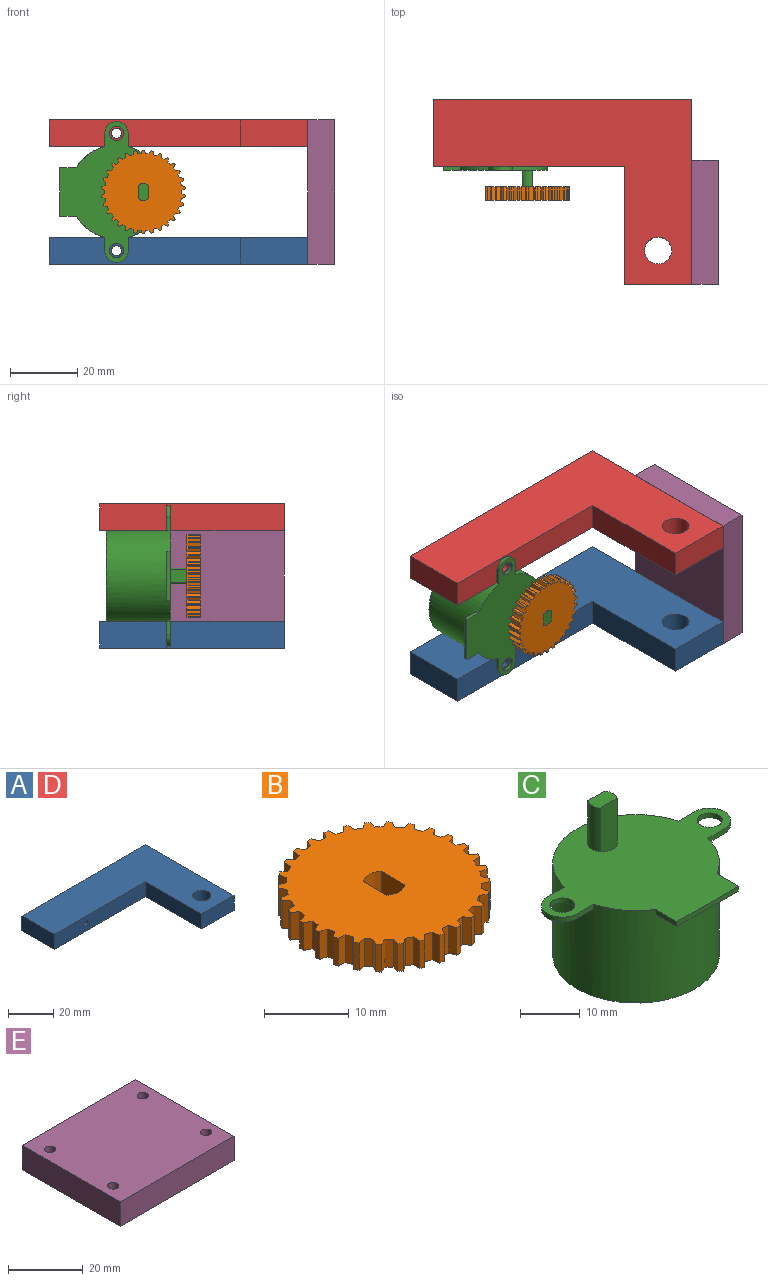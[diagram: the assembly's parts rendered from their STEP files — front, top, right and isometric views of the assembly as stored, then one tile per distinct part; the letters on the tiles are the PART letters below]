
ASSEMBLY  parts=5 mates=4
PART A: 10 faces, bbox 77x55x8 mm
  f0: plane 20x8mm, normal (0,-1,0), area 160mm2, adj f1,f5,f6,f7
  f1: plane 55x8mm, normal (1,0,0), area 440mm2, adj f0,f2,f6,f7
  f2: plane 77x8mm, normal (0,1,0), area 608.9mm2, adj f1,f3,f6,f7,f8
  f3: plane 20x8mm, normal (-1,0,0), area 160mm2, adj f2,f4,f6,f7
  f4: plane 57x8mm, normal (0,-1,0), area 448.9mm2, adj f3,f5,f6,f7,f8
  f5: plane 35x8mm, normal (-1,0,0), area 280mm2, adj f0,f4,f6,f7
  f6: plane 77x55mm, normal (0,0,1), area 2189.7mm2, adj f0,f1,f2,f3,f4,f5,f9
  f7: plane 77x55mm, normal (0,0,-1), area 2189.7mm2, adj f0,f1,f2,f3,f4,f5,f9
  f8: cylinder r=1.5mm len=20mm, axis (0,1,0), area 188.5mm2, adj f2,f4
  f9: cylinder r=4mm len=8mm, axis (0,0,-1), area 201.1mm2, adj f6,f7
PART B: 126 faces, bbox 24.9x25x4 mm
  f0: cylinder r=12.5mm len=4mm, axis (0,0,-1), area 2.6mm2, adj f30,f35,f118,f123
  f1: cylinder r=12.5mm len=4mm, axis (0,0,-1), area 2.6mm2, adj f30,f35,f54,f124
  f2: cylinder r=12.5mm len=4mm, axis (0,0,-1), area 2.6mm2, adj f30,f35,f61,f120
  f3: cylinder r=12.5mm len=4mm, axis (0,0,-1), area 2.6mm2, adj f30,f35,f111,f121
  f4: cylinder r=12.5mm len=4mm, axis (0,0,-1), area 2.6mm2, adj f30,f35,f103,f117
  f5: cylinder r=12.5mm len=4mm, axis (0,0,-1), area 2.6mm2, adj f30,f35,f100,f114
  f6: cylinder r=12.5mm len=4mm, axis (0,0,-1), area 2.6mm2, adj f30,f35,f84,f115
  f7: cylinder r=12.5mm len=4mm, axis (0,0,-1), area 2.6mm2, adj f30,f35,f39,f112
  f8: cylinder r=12.5mm len=4mm, axis (0,0,-1), area 2.6mm2, adj f30,f35,f82,f108
  f9: cylinder r=12.5mm len=4mm, axis (0,0,-1), area 2.6mm2, adj f30,f35,f78,f109
  f10: cylinder r=12.5mm len=4mm, axis (0,0,-1), area 2.6mm2, adj f30,f35,f73,f105
  f11: cylinder r=12.5mm len=4mm, axis (0,0,-1), area 2.6mm2, adj f30,f35,f45,f106
  f12: cylinder r=12.5mm len=4mm, axis (0,0,-1), area 2.6mm2, adj f30,f35,f67,f102
  f13: cylinder r=12.5mm len=4mm, axis (0,0,-1), area 2.6mm2, adj f30,f35,f79,f99
  f14: cylinder r=12.5mm len=4mm, axis (0,0,-1), area 2.6mm2, adj f30,f35,f37,f96
  f15: cylinder r=12.5mm len=4mm, axis (0,0,-1), area 2.6mm2, adj f30,f35,f87,f97
  f16: cylinder r=12.5mm len=4mm, axis (0,0,-1), area 2.6mm2, adj f30,f35,f55,f93
  f17: cylinder r=12.5mm len=4mm, axis (0,0,-1), area 2.6mm2, adj f30,f35,f48,f94
  f18: cylinder r=12.5mm len=4mm, axis (0,0,-1), area 2.6mm2, adj f30,f35,f43,f90
  f19: cylinder r=12.5mm len=4mm, axis (0,0,-1), area 2.6mm2, adj f30,f35,f69,f91
  f20: cylinder r=12.5mm len=4mm, axis (0,0,-1), area 2.6mm2, adj f30,f35,f63,f88
  f21: cylinder r=12.5mm len=4mm, axis (0,0,-1), area 2.6mm2, adj f30,f35,f36,f85
  f22: cylinder r=12.5mm len=4mm, axis (0,0,-1), area 2.6mm2, adj f30,f35,f52,f81
  f23: cylinder r=12.5mm len=4mm, axis (0,0,-1), area 2.6mm2, adj f30,f35,f40,f75
  f24: cylinder r=12.5mm len=4mm, axis (0,0,-1), area 2.6mm2, adj f30,f35,f57,f76
  f25: cylinder r=12.5mm len=4mm, axis (0,0,-1), area 2.6mm2, adj f30,f35,f49,f72
  f26: cylinder r=12.5mm len=4mm, axis (0,0,-1), area 2.6mm2, adj f30,f35,f66,f70
  f27: cylinder r=12.5mm len=4mm, axis (0,0,-1), area 2.6mm2, adj f30,f35,f42,f64
  f28: cylinder r=12.5mm len=4mm, axis (0,0,-1), area 2.6mm2, adj f30,f35,f46,f60
  f29: cylinder r=12.5mm len=4mm, axis (0,0,-1), area 2.6mm2, adj f30,f35,f51,f58
  f30: plane 25x24.92mm, normal (0,0,1), area 432.6mm2, adj f0,f1,f2,f3,f4,f5,f6,f7
  f31: cylinder r=2.5mm len=4mm, axis (0,0,-1), area 12.9mm2, adj f30,f32,f34,f35
  f32: plane 4x4mm, normal (-1,0,0), area 16mm2, adj f30,f31,f33,f35
  f33: cylinder r=2.5mm len=4mm, axis (0,0,-1), area 12.9mm2, adj f30,f32,f34,f35
  f34: plane 4x4mm, normal (1,0,0), area 16mm2, adj f30,f31,f33,f35
  f35: plane 25x24.92mm, normal (0,0,-1), area 432.6mm2, adj f0,f1,f2,f3,f4,f5,f6,f7
  f36: plane 4x1.04mm, normal (-0.96,-0.27,0), area 4.3mm2, adj f21,f30,f35,f38
  f37: plane 4x1mm, normal (0.37,0.93,0), area 4.3mm2, adj f14,f30,f35,f38
  f38: plane 4x0.74mm, normal (-0.67,0.74,0), area 4mm2, adj f30,f35,f36,f37
  f39: plane 4x1.04mm, normal (0.25,0.97,0), area 4.3mm2, adj f7,f30,f35,f41
  f40: plane 4x0.84mm, normal (0.62,-0.78,0), area 4.3mm2, adj f23,f30,f35,f41
  f41: plane 4x0.98mm, normal (0.98,0.21,0), area 4mm2, adj f30,f35,f39,f40
  f42: plane 4x0.96mm, normal (-0.45,-0.89,0), area 4.3mm2, adj f27,f30,f35,f44
  f43: plane 4x0.96mm, normal (-0.45,0.89,0), area 4.3mm2, adj f18,f30,f35,f44
  f44: plane 4x1mm, normal (-1,0,0), area 4mm2, adj f30,f35,f42,f43
  f45: plane 4x0.95mm, normal (0.89,0.46,0), area 4.3mm2, adj f11,f30,f35,f47
  f46: plane 4x1.06mm, normal (-0.16,-0.99,0), area 4.3mm2, adj f28,f30,f35,f47
  f47: plane 4x0.81mm, normal (0.81,-0.59,0), area 4mm2, adj f30,f35,f45,f46
  f48: plane 4x1.06mm, normal (0.99,-0.15,0), area 4.3mm2, adj f17,f30,f35,f50
  f49: plane 4x0.77mm, normal (-0.71,-0.7,0), area 4.3mm2, adj f25,f30,f35,f50
  f50: plane 4x0.95mm, normal (0.31,-0.95,0), area 4mm2, adj f30,f35,f48,f49
  f51: plane 4x1mm, normal (-0.37,0.93,0), area 4.3mm2, adj f29,f30,f35,f53
  f52: plane 4x1.04mm, normal (0.96,-0.27,0), area 4.3mm2, adj f22,f30,f35,f53
  f53: plane 4x0.74mm, normal (0.67,0.74,0), area 4mm2, adj f30,f35,f51,f52
  f54: plane 4x0.91mm, normal (0.84,-0.54,0), area 4.3mm2, adj f1,f30,f35,f56
  f55: plane 4x1.01mm, normal (-0.94,-0.35,0), area 4.3mm2, adj f16,f30,f35,f56
  f56: plane 4x0.99mm, normal (-0.1,-0.99,0), area 4mm2, adj f30,f35,f54,f55
  f57: plane 4x1.06mm, normal (-0.16,0.99,0), area 4.3mm2, adj f24,f30,f35,f59
  f58: plane 4x0.95mm, normal (0.89,-0.46,0), area 4.3mm2, adj f29,f30,f35,f59
  f59: plane 4x0.81mm, normal (0.81,0.59,0), area 4mm2, adj f30,f35,f57,f58
  f60: plane 4x0.83mm, normal (0.77,0.64,0), area 4.3mm2, adj f28,f30,f35,f62
  f61: plane 4x1.07mm, normal (0.04,-1,0), area 4.3mm2, adj f2,f30,f35,f62
  f62: plane 4x0.91mm, normal (0.91,-0.41,0), area 4mm2, adj f30,f35,f60,f61
  f63: plane 4x0.84mm, normal (-0.62,-0.78,0), area 4.3mm2, adj f20,f30,f35,f65
  f64: plane 4x1.04mm, normal (-0.25,0.97,0), area 4.3mm2, adj f27,f30,f35,f65
  f65: plane 4x0.98mm, normal (-0.98,0.21,0), area 4mm2, adj f30,f35,f63,f64
  f66: plane 4x1.06mm, normal (0.16,-0.99,0), area 4.3mm2, adj f26,f30,f35,f68
  f67: plane 4x0.95mm, normal (-0.89,0.46,0), area 4.3mm2, adj f12,f30,f35,f68
  f68: plane 4x0.81mm, normal (-0.81,-0.59,0), area 4mm2, adj f30,f35,f66,f67
  f69: plane 4x1.07mm, normal (-0.04,-1,0), area 4.3mm2, adj f19,f30,f35,f71
  f70: plane 4x0.83mm, normal (-0.77,0.64,0), area 4.3mm2, adj f26,f30,f35,f71
  f71: plane 4x0.91mm, normal (-0.91,-0.41,0), area 4mm2, adj f30,f35,f69,f70
  f72: plane 4x1.07mm, normal (1,0.06,0), area 4.3mm2, adj f25,f30,f35,f74
  f73: plane 4x0.9mm, normal (-0.55,-0.83,0), area 4.3mm2, adj f10,f30,f35,f74
  f74: plane 4x0.87mm, normal (0.5,-0.87,0), area 4mm2, adj f30,f35,f72,f73
  f75: plane 4x1.07mm, normal (0.04,1,0), area 4.3mm2, adj f23,f30,f35,f77
  f76: plane 4x0.83mm, normal (0.77,-0.64,0), area 4.3mm2, adj f24,f30,f35,f77
  f77: plane 4x0.91mm, normal (0.91,0.41,0), area 4mm2, adj f30,f35,f75,f76
  f78: plane 4x0.91mm, normal (-0.84,0.54,0), area 4.3mm2, adj f9,f30,f35,f80
  f79: plane 4x1.01mm, normal (0.94,0.35,0), area 4.3mm2, adj f13,f30,f35,f80
  f80: plane 4x0.99mm, normal (0.1,0.99,0), area 4mm2, adj f30,f35,f78,f79
  f81: plane 4x0.9mm, normal (-0.55,0.83,0), area 4.3mm2, adj f22,f30,f35,f83
  f82: plane 4x1.07mm, normal (1,-0.06,0), area 4.3mm2, adj f8,f30,f35,f83
  f83: plane 4x0.87mm, normal (0.5,0.87,0), area 4mm2, adj f30,f35,f81,f82
  f84: plane 4x1.07mm, normal (-1,-0.06,0), area 4.3mm2, adj f6,f30,f35,f86
  f85: plane 4x0.9mm, normal (0.55,0.83,0), area 4.3mm2, adj f21,f30,f35,f86
  f86: plane 4x0.87mm, normal (-0.5,0.87,0), area 4mm2, adj f30,f35,f84,f85
  f87: plane 4x0.83mm, normal (-0.77,-0.64,0), area 4.3mm2, adj f15,f30,f35,f89
  f88: plane 4x1.07mm, normal (-0.04,1,0), area 4.3mm2, adj f20,f30,f35,f89
  f89: plane 4x0.91mm, normal (-0.91,0.41,0), area 4mm2, adj f30,f35,f87,f88
  f90: plane 4x1.04mm, normal (-0.25,-0.97,0), area 4.3mm2, adj f18,f30,f35,f92
  f91: plane 4x0.84mm, normal (-0.62,0.78,0), area 4.3mm2, adj f19,f30,f35,f92
  f92: plane 4x0.98mm, normal (-0.98,-0.21,0), area 4mm2, adj f30,f35,f90,f91
  f93: plane 4x1.01mm, normal (0.94,-0.35,0), area 4.3mm2, adj f16,f30,f35,f95
  f94: plane 4x0.91mm, normal (-0.84,-0.54,0), area 4.3mm2, adj f17,f30,f35,f95
  f95: plane 4x0.99mm, normal (0.1,-0.99,0), area 4mm2, adj f30,f35,f93,f94
  f96: plane 4x0.95mm, normal (-0.89,-0.46,0), area 4.3mm2, adj f14,f30,f35,f98
  f97: plane 4x1.06mm, normal (0.16,0.99,0), area 4.3mm2, adj f15,f30,f35,f98
  f98: plane 4x0.81mm, normal (-0.81,0.59,0), area 4mm2, adj f30,f35,f96,f97
  f99: plane 4x1.01mm, normal (-0.94,0.35,0), area 4.3mm2, adj f13,f30,f35,f101
  f100: plane 4x0.91mm, normal (0.84,0.54,0), area 4.3mm2, adj f5,f30,f35,f101
  f101: plane 4x0.99mm, normal (-0.1,0.99,0), area 4mm2, adj f30,f35,f99,f100
  f102: plane 4x1mm, normal (0.37,-0.93,0), area 4.3mm2, adj f12,f30,f35,f104
  f103: plane 4x1.04mm, normal (-0.96,0.27,0), area 4.3mm2, adj f4,f30,f35,f104
  f104: plane 4x0.74mm, normal (-0.67,-0.74,0), area 4mm2, adj f30,f35,f102,f103
  f105: plane 4x1.04mm, normal (0.96,0.27,0), area 4.3mm2, adj f10,f30,f35,f107
  f106: plane 4x1mm, normal (-0.37,-0.93,0), area 4.3mm2, adj f11,f30,f35,f107
  f107: plane 4x0.74mm, normal (0.67,-0.74,0), area 4mm2, adj f30,f35,f105,f106
  f108: plane 4x0.77mm, normal (-0.71,0.7,0), area 4.3mm2, adj f8,f30,f35,f110
  f109: plane 4x1.06mm, normal (0.99,0.15,0), area 4.3mm2, adj f9,f30,f35,f110
  f110: plane 4x0.95mm, normal (0.31,0.95,0), area 4mm2, adj f30,f35,f108,f109
  f111: plane 4x0.96mm, normal (0.45,0.89,0), area 4.3mm2, adj f3,f30,f35,f113
  f112: plane 4x0.96mm, normal (0.45,-0.89,0), area 4.3mm2, adj f7,f30,f35,f113
  f113: plane 4x1mm, normal (1,0,0), area 4mm2, adj f30,f35,f111,f112
  f114: plane 4x1.06mm, normal (-0.99,0.15,0), area 4.3mm2, adj f5,f30,f35,f116
  f115: plane 4x0.77mm, normal (0.71,0.7,0), area 4.3mm2, adj f6,f30,f35,f116
  f116: plane 4x0.95mm, normal (-0.31,0.95,0), area 4mm2, adj f30,f35,f114,f115
  f117: plane 4x0.9mm, normal (0.55,-0.83,0), area 4.3mm2, adj f4,f30,f35,f119
  f118: plane 4x1.07mm, normal (-1,0.06,0), area 4.3mm2, adj f0,f30,f35,f119
  f119: plane 4x0.87mm, normal (-0.5,-0.87,0), area 4mm2, adj f30,f35,f117,f118
  f120: plane 4x0.84mm, normal (0.62,0.78,0), area 4.3mm2, adj f2,f30,f35,f122
  f121: plane 4x1.04mm, normal (0.25,-0.97,0), area 4.3mm2, adj f3,f30,f35,f122
  f122: plane 4x0.98mm, normal (0.98,-0.21,0), area 4mm2, adj f30,f35,f120,f121
  f123: plane 4x0.77mm, normal (0.71,-0.7,0), area 4.3mm2, adj f0,f30,f35,f125
  f124: plane 4x1.06mm, normal (-0.99,-0.15,0), area 4.3mm2, adj f1,f30,f35,f125
  f125: plane 4x0.95mm, normal (-0.31,-0.95,0), area 4mm2, adj f30,f35,f123,f124
PART C: 26 faces, bbox 42x31x28 mm
  f0: plane 7.44x7mm, normal (0,0,-1), area 30.9mm2, adj f6,f7,f8,f14,f15
  f1: plane 14.6x5.05mm, normal (0,0,-1), area 53.5mm2, adj f9,f10,f11,f15
  f2: cylinder r=2.5mm len=4mm, axis (0,0,-1), area 4.6mm2, adj f16,f20,f24
  f3: plane 3.94x1mm, normal (0,-1,0), area 3.9mm2, adj f4,f15,f16,f17
  f4: cylinder r=3.5mm len=7mm, axis (0,0,-1), area 11mm2, adj f3,f5,f16,f17
  f5: plane 3.94x1mm, normal (0,1,0), area 3.9mm2, adj f4,f15,f16,f17
  f6: plane 3.94x1mm, normal (0,1,0), area 3.9mm2, adj f0,f7,f15,f16
  f7: cylinder r=3.5mm len=7mm, axis (0,0,-1), area 11mm2, adj f0,f6,f8,f16
  f8: plane 3.94x1mm, normal (0,-1,0), area 3.9mm2, adj f0,f7,f15,f16
  f9: plane 5.05x1mm, normal (-1,0,0), area 5.1mm2, adj f1,f10,f15,f16
  f10: plane 14.6x1mm, normal (0,-1,0), area 14.6mm2, adj f1,f9,f11,f16
  f11: plane 5.05x1mm, normal (1,0,0), area 5.1mm2, adj f1,f10,f15,f16
  f12: cylinder r=2.1mm len=4.2mm, axis (0,0,-1), area 13.2mm2, adj f16,f17
  f13: cylinder r=2.5mm len=4mm, axis (0,0,-1), area 4.6mm2, adj f16,f21,f25
  f14: cylinder r=2.1mm len=4.2mm, axis (0,0,-1), area 13.2mm2, adj f0,f16
  f15: cylinder r=14mm len=28mm, axis (0,0,-1), area 1641.8mm2, adj f0,f1,f3,f5,f6,f8,f9,f11
  f16: plane 42x31mm, normal (0,0,1), area 711.4mm2, adj f2,f3,f4,f5,f6,f7,f8,f9
  f17: plane 7.44x7mm, normal (0,0,-1), area 30.9mm2, adj f3,f4,f5,f12,f15
  f18: cylinder r=2.5mm len=9mm, axis (0,0,-1), area 29mm2, adj f16,f20,f21,f22
  f19: cylinder r=2.5mm len=9mm, axis (0,0,-1), area 29mm2, adj f16,f20,f21,f22
  f20: plane 10x4mm, normal (0,1,0), area 40mm2, adj f2,f18,f19,f22,f24
  f21: plane 10x4mm, normal (0,-1,0), area 40mm2, adj f13,f18,f19,f22,f25
  f22: plane 5x3mm, normal (0,0,1), area 14mm2, adj f18,f19,f20,f21
  f23: plane 28x28mm, normal (0,0,-1), area 615.8mm2, adj f15
  f24: plane 4x1mm, normal (0,0,1), area 2.8mm2, adj f2,f20
  f25: plane 4x1mm, normal (0,0,1), area 2.8mm2, adj f13,f21
PART D: same geometry as A
PART E: 10 faces, bbox 43x37x8 mm
  f0: plane 43x8mm, normal (0,1,0), area 344mm2, adj f1,f7,f8,f9
  f1: plane 37x8mm, normal (-1,0,0), area 296mm2, adj f0,f2,f8,f9
  f2: plane 43x8mm, normal (0,-1,0), area 344mm2, adj f1,f7,f8,f9
  f3: cylinder r=1.5mm len=8mm, axis (0,0,-1), area 75.4mm2, adj f8,f9
  f4: cylinder r=1.5mm len=8mm, axis (0,0,-1), area 75.4mm2, adj f8,f9
  f5: cylinder r=1.5mm len=8mm, axis (0,0,-1), area 75.4mm2, adj f8,f9
  f6: cylinder r=1.5mm len=8mm, axis (0,0,-1), area 75.4mm2, adj f8,f9
  f7: plane 37x8mm, normal (1,0,0), area 296mm2, adj f0,f2,f8,f9
  f8: plane 43x37mm, normal (0,0,1), area 1562.7mm2, adj f0,f1,f2,f3,f4,f5,f6,f7
  f9: plane 43x37mm, normal (0,0,-1), area 1562.7mm2, adj f0,f1,f2,f3,f4,f5,f6,f7
PLACE A t=(-295.01,237.62,-39)mm
PLACE B rot(axis=(-1,0,0),90deg) t=(-332.02,232.62,-17.5)mm
PLACE C rot(axis=(0.58,0.58,-0.58),120deg) t=(-340.02,242.62,-17.5)mm
PLACE D t=(-295.01,237.62,-4)mm
PLACE E rot(axis=(0,1,0),90deg) t=(-283.02,226.12,-17.5)mm
MATE fastened A.f9 <-> D.f9  axis (0,0,-1) through (-293.02,217.62,-31)mm
MATE fastened C.f14 <-> D.f8  axis (0,-1,0) through (-340.02,241.62,0)mm
MATE fastened E.f9 <-> D.f1  axis (-1,0,0) through (-283.02,207.62,4)mm
MATE fastened B.f33 <-> C.f19  axis (0,-1,0) through (-332.02,232.62,-17.5)mm
